# Revit family: FU_Table_Sandler_590AQ-XT
name_source: partatom
category: Furniture
units: mm (PartAtom-declared; Revit-internal decimal feet)

## family parameters
Always vertical = Yes
Cut with Voids When Loaded = No
OmniClass Number = 23.40.20.00
OmniClass Title = General Furniture and Specialties
Room Calculation Point = No
Shared = No
Work Plane-Based = No

## types (5) — shared parameters
Depth = 400 mm  [stored 1.31234 ft]
Description = Double column table base in stainless steel.
Elevation = 720 mm  [stored 2.3622 ft]
Height = 720 mm  [stored 2.3622 ft]
Manufacturer = Sandler
Model = 590Q-MT
URL = https://www.sandlerseating.com
Width = 750 mm  [stored 2.46063 ft]
zero-valued in all types: Default Elevation

## per-type parameters (varying)
| type | Top Size |
| 590Q-MT - 28x48" Top (70x120cm) | FU_TableTops_MT Sqr : 28x48" Top (70x120cm) |
| 590Q-MT - 28x51" Top (70x130cm) | FU_TableTops_MT Sqr : 28x52" Top (70x130cm) |
| 590Q-MT - 32x48" Top (80x120cm) | FU_TableTops_MT Sqr : 32x48" Top (80x120cm) |
| 590Q-MT - 32x51" Top (80x130cm) | FU_TableTops_MT Sqr : 32x52" Top (80x130cm) |
| 590Q-MT - 32x56" Top (80x140cm) | FU_TableTops_MT Sqr : 32x55" Top (80x140cm) |

note: [stored X ft] marks values corroborated as IEEE doubles in the binary element streams (Revit-internal decimal feet)

## geometry (parser evidence)
native form markers: Sweep x3
no freeform markers — native parametric forms only
